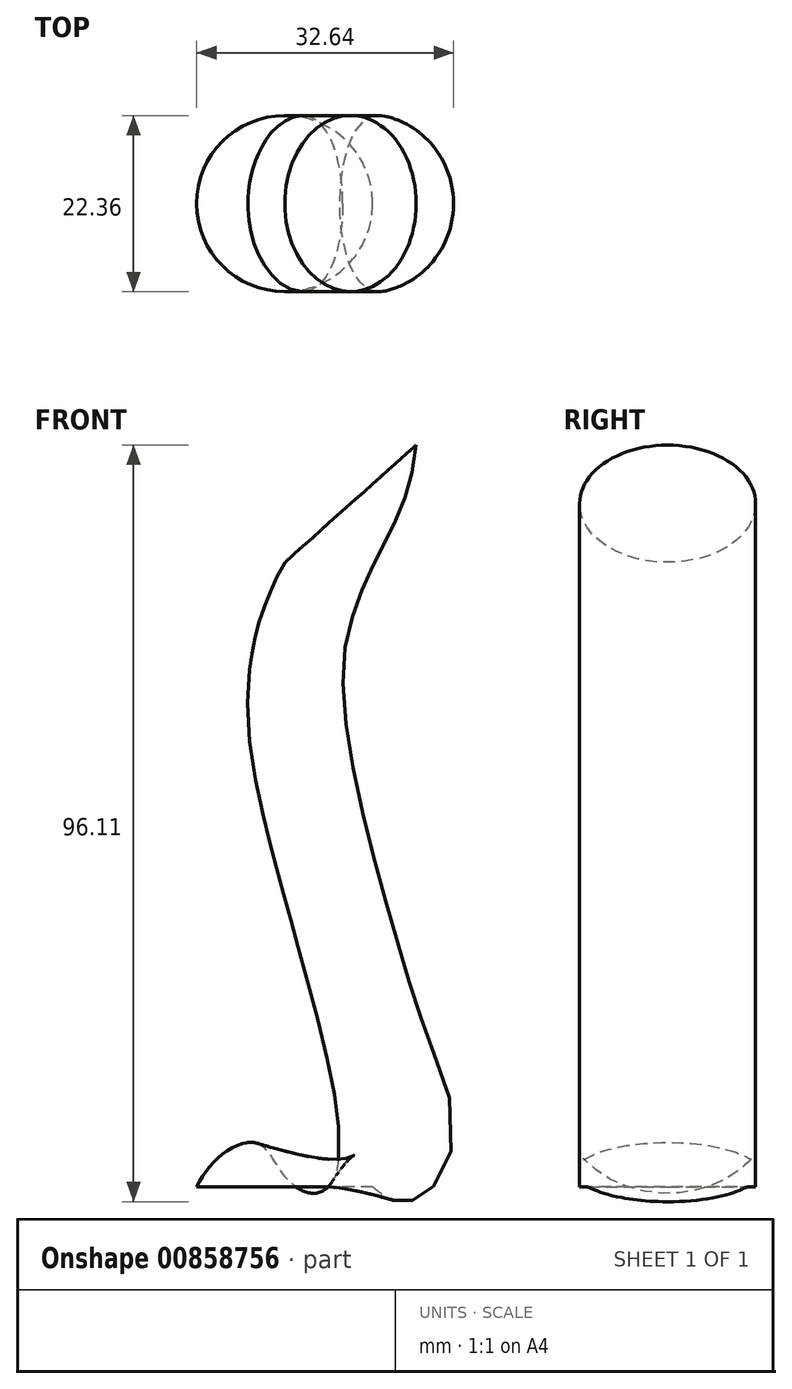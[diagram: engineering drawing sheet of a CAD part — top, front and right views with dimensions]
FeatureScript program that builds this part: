
annotation { "Feature Type Name" : "Feature", "Feature Type Description" : "" }
export const myFeature = defineFeature(function(context is Context, id is Id, definition is map)
    precondition{}
    {
        {
            var Q0;
            Q0=qCreatedBy(makeId("Top.planeOp"),FACE);
            var sketch = newSketch(context, id + "F0", { "sketchPlane" : qUnion([Q0])});
            skCircle(sketch, "E0", {"center": v(-62.28, 52.52) * mm, "radius": 11.18 * mm});
            skSolve(sketch);
        }
        {
            var Q0;
            Q0=sQuery(id+"F0.wireOp",VERTEX,"E0.center");
            var Q1;
            Q1=qCreatedBy(makeId("Front.planeOp"),FACE);
            cPlane(context, id + "F1", {"entities" : qUnion([Q0, Q1]), "cplaneType" : CPlaneType.PLANE_POINT, "offset" : 25.4 * mm, "width" : 152.4 * mm, "height" : 152.4 * mm});
        }
        {
            var Q0;
            Q0=qCreatedBy(id+"F1.planeOp",FACE);
            var sketch = newSketch(context, id + "F2", { "sketchPlane" : qUnion([Q0])});
            skFitSpline(sketch, "E1", {"points": [v(-62.62, 0) * mm, v(-51.24, 5.33) * mm, v(-60.15, 58.08) * mm, v(-54.17, 86.54) * mm], "startDerivative": vector(55.92, 35.8) * mm, "endDerivative": vector(20.35, 72.92) * mm});
            skSolve(sketch);
        }
        {
            var Q0;
            Q0=makeQuery(id+"F0.imprint","IMPRINT",FACE,{"disambiguationData":[TD([[makeQuery(id+"F0.imprint","IMPRINT",EDGE,{"derivedFrom":sQuery(id+"F0.wireOp",EDGE,"E0")}),1.0]])]});
            var Q1;
            Q1=sQuery(id+"F2.wireOp",EDGE,"E1");
            sweep(context, id + "F3", {"profiles" : qUnion([Q0]), "path" : qUnion([Q1])});
        }
    });
